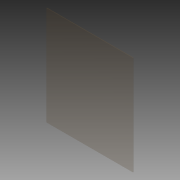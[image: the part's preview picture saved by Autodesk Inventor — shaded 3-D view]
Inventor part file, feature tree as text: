
AUTODESK INVENTOR PART (.ipt)
format: ipt  version: 2012 (Build 160160000, 160)  size: 67,072 bytes
history: native  units: in
note: dims shown in document units (in); Inventor stores cm internally (conversion verified against a paired STEP export)
features: extrude x1, sketch x1
ambient origin geometry x8: Origin, YZ Plane, XZ Plane, XY Plane, X Axis, Y Axis, Z Axis, Center Point
bodies: Solid1 (feature_tree)
feature tree (2):
  extrude  "Extrusion1"  Depth=14.875in
  sketch  "Sketch1"  dims[d0=17.0in d1=14.875in d2=0.125in d3=0.0in]
